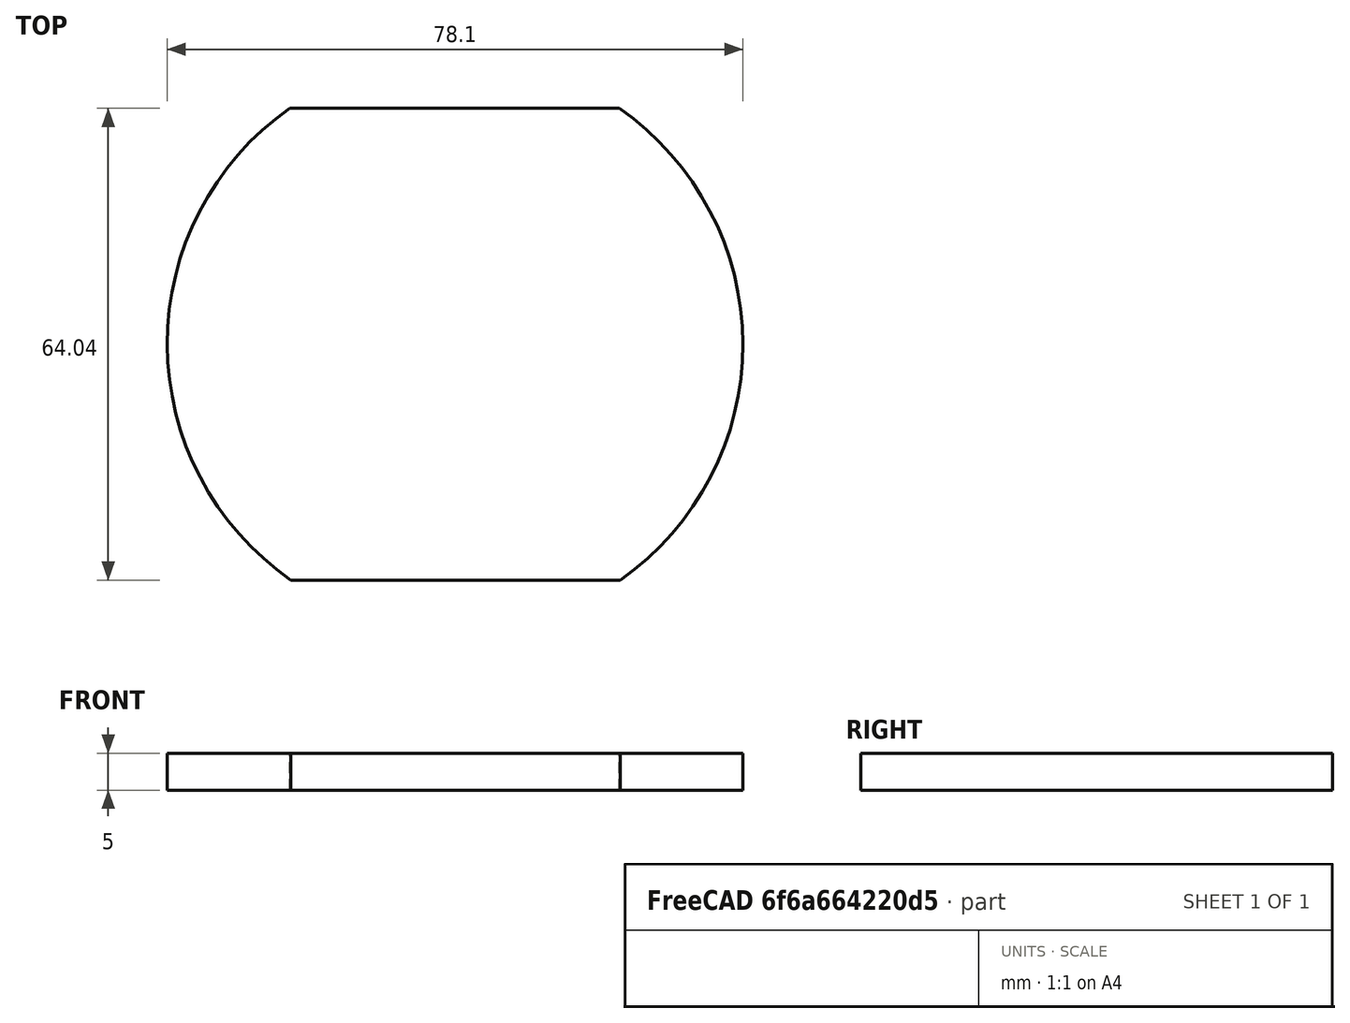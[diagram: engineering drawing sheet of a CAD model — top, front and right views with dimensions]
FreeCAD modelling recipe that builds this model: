
FCSTD DOCUMENT  (FreeCAD 1.0R39319 (Git))
Label: chapa_chord_cut_FINAL
License: All rights reserved
LicenseURL: https://en.wikipedia.org/wiki/All_rights_reserved
objects: Sketcher::SketchObject×1, PartDesign::Pad×1, PartDesign::Body×1
note: 6 computed .brp shape members not serialized (recipe doc carries the construction recipe); baked Part::Feature solids carry a one-line shape summary decoded from their .brp

FEATURE [Sketcher::SketchObject] Sketch_1
  ArcFitTolerance = 1e-06
  AttachmentSupport = -> [XY_Plane]
  FullyConstrained = false
  MakeInternals = false
  MapMode = 5
  sketch-geometry (4):
    g0: ArcOfCircle CenterX=-0.00133786 CenterY=-6.76527 CenterZ=0 NormalX=0 NormalY=0 NormalZ=1 AngleXU=0 Radius=39.0492 StartAngle=5.32437 EndAngle=7.24728
    g1: LineSegment StartX=22.2631 StartY=25.3148 StartZ=0 EndX=-22.4327 EndY=25.3148 EndZ=0
    g2: ArcOfCircle CenterX=0.00210096 CenterY=-6.64716 CenterZ=0 NormalX=0 NormalY=0 NormalZ=1 AngleXU=0 Radius=39.0498 StartAngle=2.18281 EndAngle=4.10567
    g3: LineSegment StartX=-22.2631 StartY=-38.7275 StartZ=0 EndX=22.4319 EndY=-38.7275 EndZ=0
  constraints (7):
    c: Coincident(g0,g1)
    c: Coincident(g1,g2)
    c: Coincident(g2,g3)
    c: Coincident(g3,g0)
    c: Parallel(g1,g3)
    c: Horizontal(g1)
    c: Distance(g1,g3) = 78
FEATURE [PartDesign::Pad] Pad_1
  Direction = (0,0,1)
  Length = 5
  Length2 = 10
  Profile = -> Sketch_1
  Refine = true
  Suppressed = false
  Type = 0
FEATURE [PartDesign::Body] Body
  AllowCompound = false
  Group = -> [Sketch_1,Pad_1]
  Origin = -> Origin
  Tip = -> Pad_1
